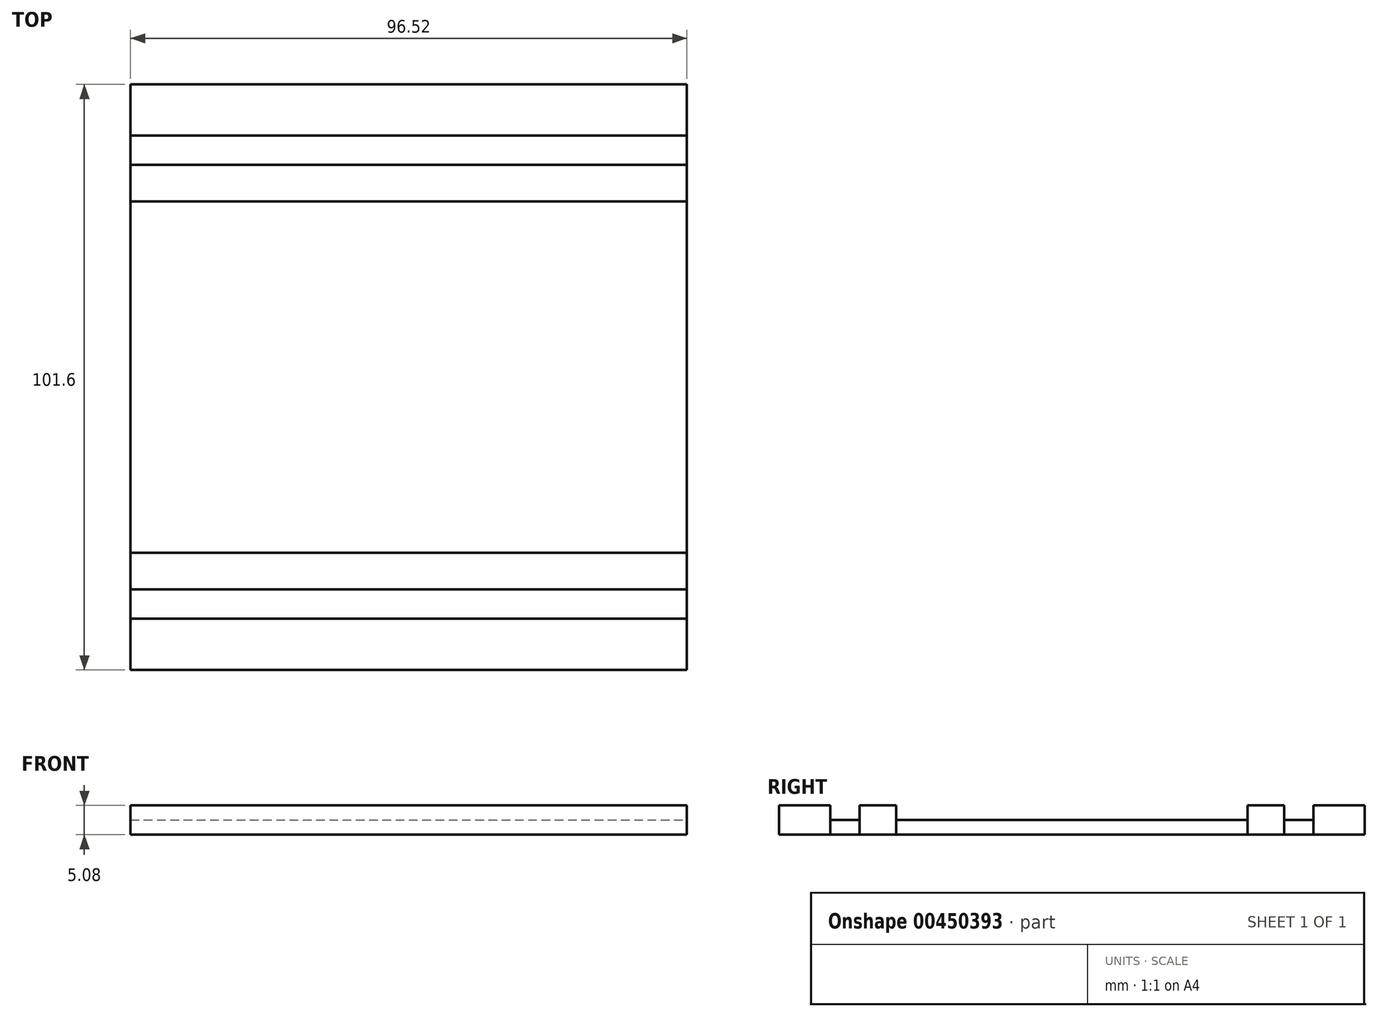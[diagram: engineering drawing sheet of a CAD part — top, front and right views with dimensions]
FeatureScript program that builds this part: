
annotation { "Feature Type Name" : "Feature", "Feature Type Description" : "" }
export const myFeature = defineFeature(function(context is Context, id is Id, definition is map)
    precondition{}
    {
        {
            var Q0;
            Q0=qCreatedBy(makeId("Top.planeOp"),FACE);
            var sketch = newSketch(context, id + "F0", { "sketchPlane" : qUnion([Q0])});
            skLineSegment(sketch, "E0.bottom", {"start": v(48.26, -50.8) * mm, "end": v(-48.26, -50.8) * mm});
            skLineSegment(sketch, "E0.top", {"start": v(48.26, 50.8) * mm, "end": v(-48.26, 50.8) * mm});
            skLineSegment(sketch, "E0.left", {"start": v(48.26, -50.8) * mm, "end": v(48.26, 50.8) * mm});
            skLineSegment(sketch, "E0.right", {"start": v(-48.26, -50.8) * mm, "end": v(-48.26, 50.8) * mm});
            skPoint(sketch, "E0.middle", {"position": v(0, 0) * mm});
            skLineSegment(sketch, "E1", {"start": v(-48.26, 36.83) * mm, "end": v(48.26, 36.83) * mm});
            skLineSegment(sketch, "E2", {"start": v(-48.26, -36.83) * mm, "end": v(48.26, -36.83) * mm});
            skLineSegment(sketch, "E3", {"start": v(-48.26, -41.91) * mm, "end": v(48.26, -41.91) * mm});
            skLineSegment(sketch, "E4", {"start": v(-48.26, 41.91) * mm, "end": v(48.26, 41.91) * mm});
            skLineSegment(sketch, "E5", {"start": v(-48.26, -30.48) * mm, "end": v(48.26, -30.48) * mm});
            skLineSegment(sketch, "E6", {"start": v(-48.26, 30.48) * mm, "end": v(48.26, 30.48) * mm});
            skSolve(sketch);
        }
        {
            var Q0;
            {var subQ0=sQuery(id+"F0.wireOp",EDGE,"E0.top");Q0=makeQuery(id+"F0.imprint","IMPRINT",FACE,{"disambiguationData":[TD([[makeQuery(id+"F0.imprint","IMPRINT",EDGE,{"derivedFrom":subQ0}),1.0]])]});}
            var Q1;
            {var subQ0=sQuery(id+"F0.wireOp",EDGE,"E1");Q1=makeQuery(id+"F0.imprint","IMPRINT",FACE,{"disambiguationData":[TD([[makeQuery(id+"F0.imprint","IMPRINT",EDGE,{"derivedFrom":subQ0}),-1.0]])]});}
            var Q2;
            {var subQ0=sQuery(id+"F0.wireOp",EDGE,"E0.bottom");Q2=makeQuery(id+"F0.imprint","IMPRINT",FACE,{"disambiguationData":[TD([[makeQuery(id+"F0.imprint","IMPRINT",EDGE,{"derivedFrom":subQ0}),-1.0]])]});}
            var Q3;
            {var subQ0=sQuery(id+"F0.wireOp",EDGE,"E2");Q3=makeQuery(id+"F0.imprint","IMPRINT",FACE,{"disambiguationData":[TD([[makeQuery(id+"F0.imprint","IMPRINT",EDGE,{"derivedFrom":subQ0}),1.0]])]});}
            extrude(context, id + "F1", {"entities" : qUnion([Q0, Q1, Q2, Q3]), "depth" : 5.08 * mm, "offsetDistance" : 25.4 * mm});
        }
        {
            var Q0;
            {var subQ0=sQuery(id+"F0.wireOp",EDGE,"E1");Q0=makeQuery(id+"F0.imprint","IMPRINT",FACE,{"disambiguationData":[TD([[makeQuery(id+"F0.imprint","IMPRINT",EDGE,{"derivedFrom":subQ0}),1.0]])]});}
            var Q1;
            {var subQ0=sQuery(id+"F0.wireOp",EDGE,"E2");Q1=makeQuery(id+"F0.imprint","IMPRINT",FACE,{"disambiguationData":[TD([[makeQuery(id+"F0.imprint","IMPRINT",EDGE,{"derivedFrom":subQ0}),-1.0]])]});}
            var Q2;
            {var subQ0=sQuery(id+"F0.wireOp",EDGE,"E5");Q2=makeQuery(id+"F0.imprint","IMPRINT",FACE,{"disambiguationData":[TD([[makeQuery(id+"F0.imprint","IMPRINT",EDGE,{"derivedFrom":subQ0}),1.0]])]});}
            extrude(context, id + "F2", {"entities" : qUnion([Q0, Q1, Q2]), "depth" : 2.54 * mm, "offsetDistance" : 25.4 * mm});
        }
    });
